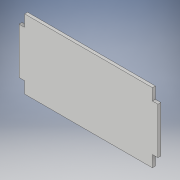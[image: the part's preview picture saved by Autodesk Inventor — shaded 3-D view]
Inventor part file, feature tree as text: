
AUTODESK INVENTOR PART (.ipt)
format: ipt  version: 2019 (Build 230136000, 136)  size: 103,424 bytes
history: native  units: mm
features: extrude x1, sketch x1
ambient origin geometry x8: Origin, YZ Plane, XZ Plane, XY Plane, X Axis, Y Axis, Z Axis, Center Point
bodies: Solid1 (feature_tree)
feature tree (2):
  extrude  "Extrusion1"  Depth=138.0mm
  sketch  "Sketch1"  dims[d0=75.0mm d1=138.0mm d2=50.0mm d3=50.0mm d4=12.5mm d5=12.5mm d8=3.2mm d9=0.0mm d10=6.0mm d11=6.0mm]
